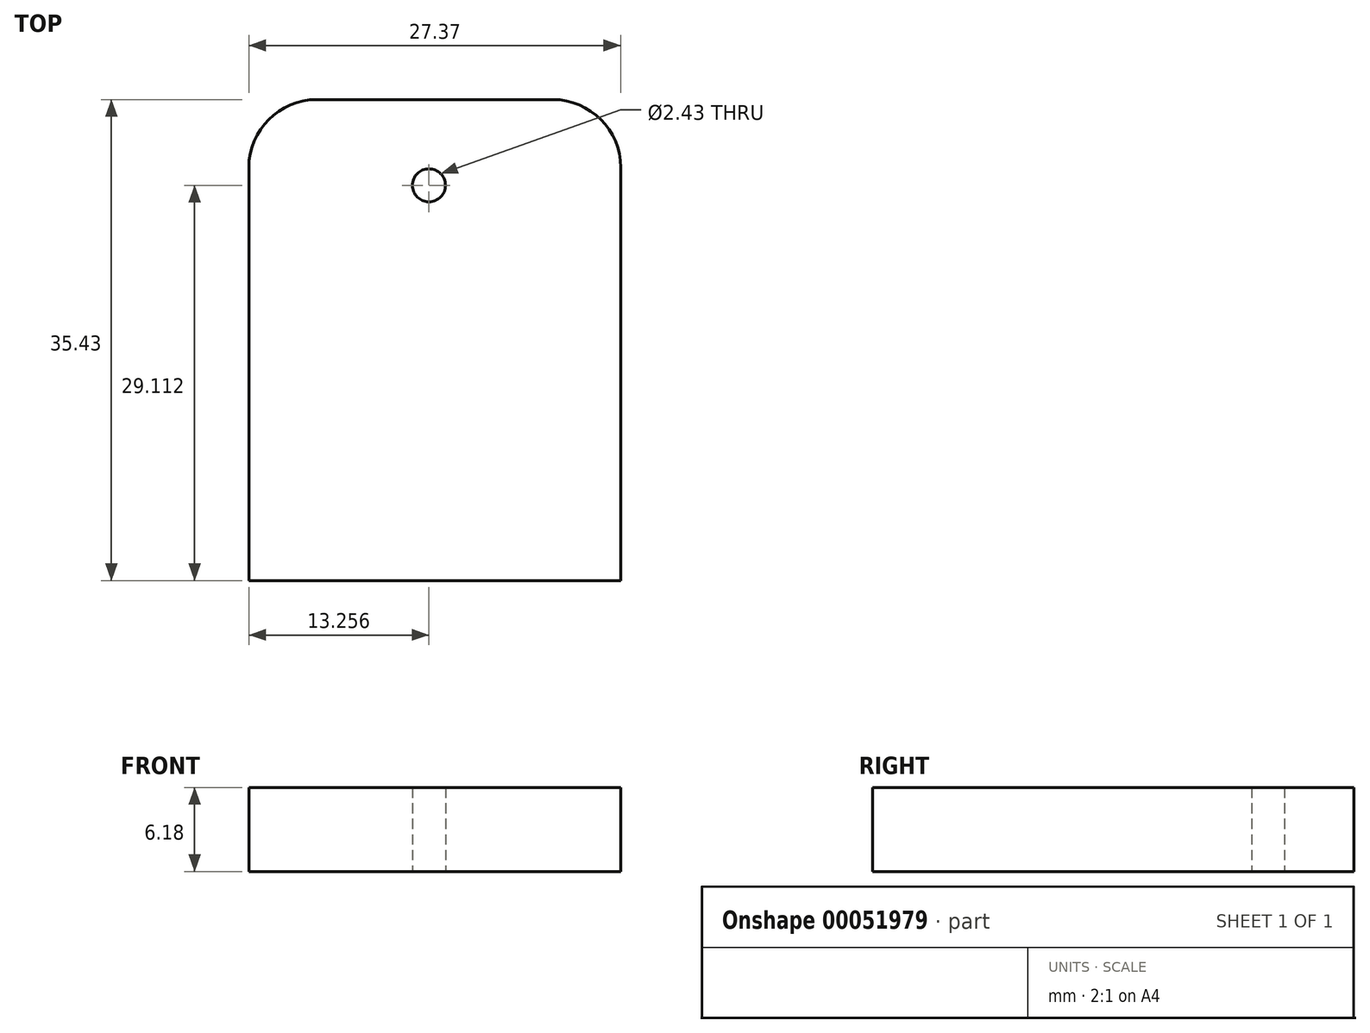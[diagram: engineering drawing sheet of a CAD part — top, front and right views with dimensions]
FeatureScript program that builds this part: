
annotation { "Feature Type Name" : "Feature", "Feature Type Description" : "" }
export const myFeature = defineFeature(function(context is Context, id is Id, definition is map)
    precondition{}
    {
        {
            var Q0;
            Q0=qCreatedBy(makeId("Top.planeOp"),FACE);
            var sketch = newSketch(context, id + "F0", { "sketchPlane" : qUnion([Q0])});
            skLineSegment(sketch, "E0.bottom", {"start": v(-48.31, 49.76) * mm, "end": v(-20.94, 49.76) * mm});
            skLineSegment(sketch, "E0.top", {"start": v(-48.31, 14.33) * mm, "end": v(-20.94, 14.33) * mm});
            skLineSegment(sketch, "E0.left", {"start": v(-48.31, 49.76) * mm, "end": v(-48.31, 14.33) * mm});
            skLineSegment(sketch, "E0.right", {"start": v(-20.94, 49.76) * mm, "end": v(-20.94, 14.33) * mm});
            skSolve(sketch);
        }
        {
            var Q0;
            Q0 = qSketchRegion(id + "F0", true);
            extrude(context, id + "F1", {"entities" : qUnion([Q0]), "depth" : 6.18 * mm});
        }
        {
            var Q0;
            Q0=makeQuery(id+"F1.opExtrude","SWEPT_EDGE",EDGE,{"disambiguationData":[OSD([sQuery(id+"F0.wireOp",EDGE,"E0.bottom"),sQuery(id+"F0.wireOp",EDGE,"E0.right")])]});
            var Q1;
            Q1=makeQuery(id+"F1.opExtrude","SWEPT_EDGE",EDGE,{"disambiguationData":[OSD([sQuery(id+"F0.wireOp",EDGE,"E0.bottom"),sQuery(id+"F0.wireOp",EDGE,"E0.left")])]});
            fillet(context, id + "F2", {"entities" : qUnion([Q0, Q1]), "radius" : 5 * mm, "tangentPropagation" : true, "allowEdgeOverflow" : false});
        }
        {
            var Q0;
            Q0=qCreatedBy(makeId("Top.planeOp"),FACE);
            var sketch = newSketch(context, id + "F3", { "sketchPlane" : qUnion([Q0])});
            skCircle(sketch, "E1", {"center": v(-35.05, 43.44) * mm, "radius": 1.22 * mm});
            skSolve(sketch);
        }
        {
            var Q0;
            Q0 = qSketchRegion(id + "F3", true);
            extrude(context, id + "F4", {"entities" : qUnion([Q0]), "operationType" : NewBodyOperationType.REMOVE, "depth" : 25 * mm});
        }
    });
